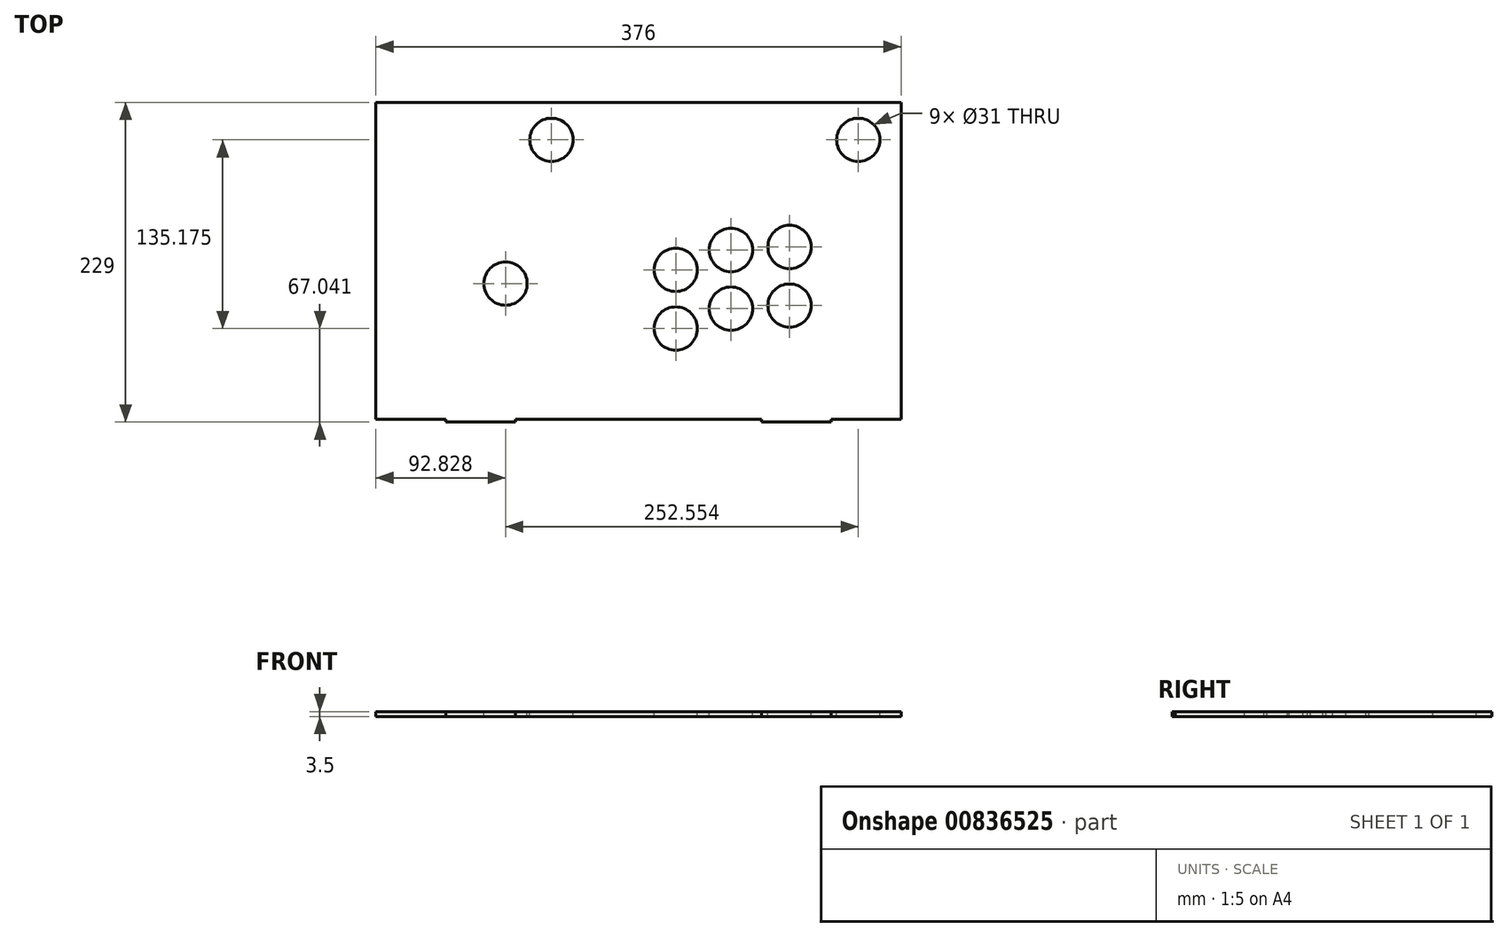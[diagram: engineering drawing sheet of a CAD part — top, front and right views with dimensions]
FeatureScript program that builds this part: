
annotation { "Feature Type Name" : "Feature", "Feature Type Description" : "" }
export const myFeature = defineFeature(function(context is Context, id is Id, definition is map)
    precondition{}
    {
        {
            var Q0;
            Q0=qCreatedBy(makeId("Top.planeOp"),FACE);
            var sketch = newSketch(context, id + "F0", { "sketchPlane" : qUnion([Q0])});
            skLineSegment(sketch, "E0.bottom", {"start": v(0, 0) * mm, "end": v(376, 0) * mm});
            skLineSegment(sketch, "E0.top", {"start": v(0, 227) * mm, "end": v(376, 227) * mm});
            skLineSegment(sketch, "E0.left", {"start": v(0, 0) * mm, "end": v(0, 227) * mm});
            skLineSegment(sketch, "E0.right", {"start": v(376, 0) * mm, "end": v(376, 227) * mm});
            skSolve(sketch);
        }
        {
            var Q0;
            Q0=makeQuery(id+"F0.imprint","IMPRINT",FACE,{"disambiguationData":[TD([[makeQuery(id+"F0.imprint","IMPRINT",EDGE,{"derivedFrom":sQuery(id+"F0.wireOp",EDGE,"E0.bottom")}),1.0]])]});
            extrude(context, id + "F1", {"entities" : qUnion([Q0]), "depth" : 3.5 * mm, "offsetDistance" : 25 * mm});
        }
        {
            var Q0;
            Q0=makeQuery(id+"F1.opExtrude","CAP_FACE",FACE,{"disambiguationData":[OSD([sQuery(id+"F0.wireOp",EDGE,"E0.bottom"),sQuery(id+"F0.wireOp",EDGE,"E0.top"),sQuery(id+"F0.wireOp",EDGE,"E0.left"),sQuery(id+"F0.wireOp",EDGE,"E0.right")])],"isStart":false});
            var sketch = newSketch(context, id + "F2", { "sketchPlane" : qUnion([Q0])});
            skCircle(sketch, "E1", {"center": v(214.7, 107.04) * mm, "radius": 15.5 * mm});
            skCircle(sketch, "E2", {"center": v(214.7, 65.04) * mm, "radius": 15.5 * mm});
            skCircle(sketch, "E3", {"center": v(254.22, 121.27) * mm, "radius": 15.5 * mm});
            skCircle(sketch, "E4", {"center": v(254.22, 79.27) * mm, "radius": 15.5 * mm});
            skCircle(sketch, "E5", {"center": v(296.16, 81.47) * mm, "radius": 15.5 * mm});
            skCircle(sketch, "E6", {"center": v(296.16, 123.47) * mm, "radius": 15.5 * mm});
            skCircle(sketch, "E7", {"center": v(92.83, 97.23) * mm, "radius": 15.5 * mm});
            skCircle(sketch, "E8", {"center": v(345.38, 200.22) * mm, "radius": 15.5 * mm});
            skCircle(sketch, "E9", {"center": v(125.7, 200.22) * mm, "radius": 15.5 * mm});
            skSolve(sketch);
        }
        {
            var Q0;
            Q0=makeQuery(id+"F2.imprint","IMPRINT",FACE,{"disambiguationData":[TD([[makeQuery(id+"F2.imprint","IMPRINT",EDGE,{"derivedFrom":sQuery(id+"F2.wireOp",EDGE,"E7")}),1.0]])]});
            var Q1;
            Q1=makeQuery(id+"F2.imprint","IMPRINT",FACE,{"disambiguationData":[TD([[makeQuery(id+"F2.imprint","IMPRINT",EDGE,{"derivedFrom":sQuery(id+"F2.wireOp",EDGE,"E9")}),1.0]])]});
            var Q2;
            Q2=makeQuery(id+"F2.imprint","IMPRINT",FACE,{"disambiguationData":[TD([[makeQuery(id+"F2.imprint","IMPRINT",EDGE,{"derivedFrom":sQuery(id+"F2.wireOp",EDGE,"E1")}),1.0]])]});
            var Q3;
            Q3=makeQuery(id+"F2.imprint","IMPRINT",FACE,{"disambiguationData":[TD([[makeQuery(id+"F2.imprint","IMPRINT",EDGE,{"derivedFrom":sQuery(id+"F2.wireOp",EDGE,"E2")}),1.0]])]});
            var Q4;
            Q4=makeQuery(id+"F2.imprint","IMPRINT",FACE,{"disambiguationData":[TD([[makeQuery(id+"F2.imprint","IMPRINT",EDGE,{"derivedFrom":sQuery(id+"F2.wireOp",EDGE,"E4")}),1.0]])]});
            var Q5;
            Q5=makeQuery(id+"F2.imprint","IMPRINT",FACE,{"disambiguationData":[TD([[makeQuery(id+"F2.imprint","IMPRINT",EDGE,{"derivedFrom":sQuery(id+"F2.wireOp",EDGE,"E3")}),1.0]])]});
            var Q6;
            Q6=makeQuery(id+"F2.imprint","IMPRINT",FACE,{"disambiguationData":[TD([[makeQuery(id+"F2.imprint","IMPRINT",EDGE,{"derivedFrom":sQuery(id+"F2.wireOp",EDGE,"E6")}),1.0]])]});
            var Q7;
            Q7=makeQuery(id+"F2.imprint","IMPRINT",FACE,{"disambiguationData":[TD([[makeQuery(id+"F2.imprint","IMPRINT",EDGE,{"derivedFrom":sQuery(id+"F2.wireOp",EDGE,"E5")}),1.0]])]});
            var Q8;
            Q8=makeQuery(id+"F2.imprint","IMPRINT",FACE,{"disambiguationData":[TD([[makeQuery(id+"F2.imprint","IMPRINT",EDGE,{"derivedFrom":sQuery(id+"F2.wireOp",EDGE,"E8")}),1.0]])]});
            extrude(context, id + "F3", {"entities" : qUnion([Q0, Q1, Q2, Q3, Q4, Q5, Q6, Q7, Q8]), "operationType" : NewBodyOperationType.REMOVE, "oppositeDirection" : true, "depth" : 25 * mm, "offsetDistance" : 25 * mm});
        }
        {
            var Q0;
            Q0=makeQuery(id+"F0.imprint","IMPRINT",FACE,{"disambiguationData":[TD([[makeQuery(id+"F0.imprint","IMPRINT",EDGE,{"derivedFrom":sQuery(id+"F0.wireOp",EDGE,"E0.bottom")}),1.0]])]});
            var sketch = newSketch(context, id + "F4", { "sketchPlane" : qUnion([Q0])});
            skLineSegment(sketch, "E10", {"start": v(0, 227) * mm, "end": v(376, 227) * mm});
            skLineSegment(sketch, "E11", {"start": v(376, 227) * mm, "end": v(376, 0) * mm});
            skLineSegment(sketch, "E12", {"start": v(376, 0) * mm, "end": v(0, 0) * mm});
            skLineSegment(sketch, "E13", {"start": v(0, 0) * mm, "end": v(0, 227) * mm});
            skSolve(sketch);
        }
        {
            var Q0;
            Q0=makeQuery(id+"F2.imprint","IMPRINT",FACE,{"disambiguationData":[TD([[makeQuery(id+"F2.imprint","IMPRINT",EDGE,{"derivedFrom":sQuery(id+"F2.wireOp",EDGE,"E1")}),-1.0]])]});
            var sketch = newSketch(context, id + "F5", { "sketchPlane" : qUnion([Q0])});
            skLineSegment(sketch, "E14.bottom", {"start": v(50, 0) * mm, "end": v(100, 0) * mm});
            skLineSegment(sketch, "E14.top", {"start": v(50, -2) * mm, "end": v(100, -2) * mm});
            skLineSegment(sketch, "E14.left", {"start": v(50, 0) * mm, "end": v(50, -2) * mm});
            skLineSegment(sketch, "E14.right", {"start": v(100, 0) * mm, "end": v(100, -2) * mm});
            skLineSegment(sketch, "E15.bottom", {"start": v(276, 0) * mm, "end": v(326, 0) * mm});
            skLineSegment(sketch, "E15.top", {"start": v(276, -2) * mm, "end": v(326, -2) * mm});
            skLineSegment(sketch, "E15.left", {"start": v(276, 0) * mm, "end": v(276, -2) * mm});
            skLineSegment(sketch, "E15.right", {"start": v(326, 0) * mm, "end": v(326, -2) * mm});
            skSolve(sketch);
        }
        {
            var Q0;
            Q0 = qSketchRegion(id + "F5", true);
            extrude(context, id + "F6", {"entities" : qUnion([Q0]), "operationType" : NewBodyOperationType.ADD, "oppositeDirection" : true, "depth" : 3.5 * mm, "offsetDistance" : 25 * mm});
        }
    });
